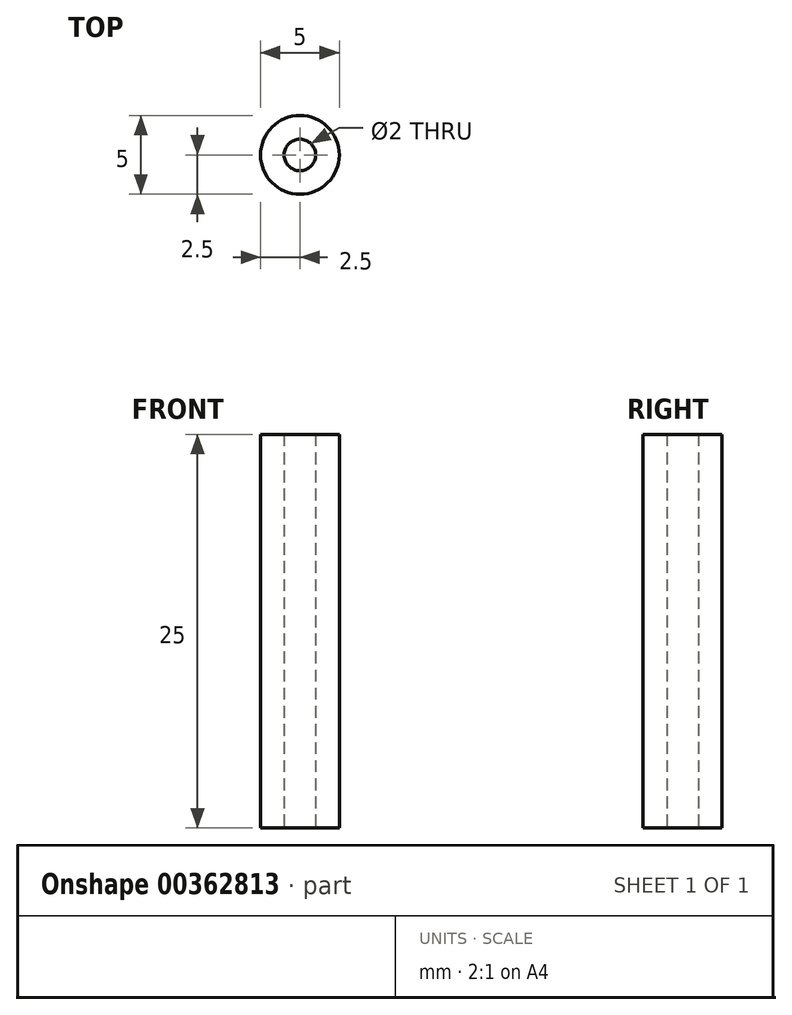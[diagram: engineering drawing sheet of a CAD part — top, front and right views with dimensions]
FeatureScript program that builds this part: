
annotation { "Feature Type Name" : "Feature", "Feature Type Description" : "" }
export const myFeature = defineFeature(function(context is Context, id is Id, definition is map)
    precondition{}
    {
        {
            var Q0;
            Q0=qCreatedBy(makeId("Top.planeOp"),FACE);
            var sketch = newSketch(context, id + "F0", { "sketchPlane" : qUnion([Q0])});
            skCircle(sketch, "E0", {"center": v(0, 0) * mm, "radius": 2.5 * mm});
            skCircle(sketch, "E1", {"center": v(0, 0) * mm, "radius": 1 * mm});
            skSolve(sketch);
        }
        {
            var Q0;
            Q0=makeQuery(id+"F0.imprint","IMPRINT",FACE,{"disambiguationData":[TD([[makeQuery(id+"F0.imprint","IMPRINT",EDGE,{"derivedFrom":sQuery(id+"F0.wireOp",EDGE,"E0")}),1.0]])]});
            extrude(context, id + "F1", {"entities" : qUnion([Q0]), "depth" : 1 * mm});
        }
        {
            var Q0;
            Q0 = qSketchRegion(id + "F0", true);
            var Q1;
            Q1=makeQuery(id+"F1.opExtrude","CAP_FACE",FACE,{"disambiguationData":[OSD([sQuery(id+"F0.wireOp",EDGE,"E0"),sQuery(id+"F0.wireOp",EDGE,"E1")])],"isStart":true});
            extrude(context, id + "F2", {"entities" : qUnion([Q0, Q1]), "operationType" : NewBodyOperationType.ADD, "depth" : 25 * mm});
        }
    });
